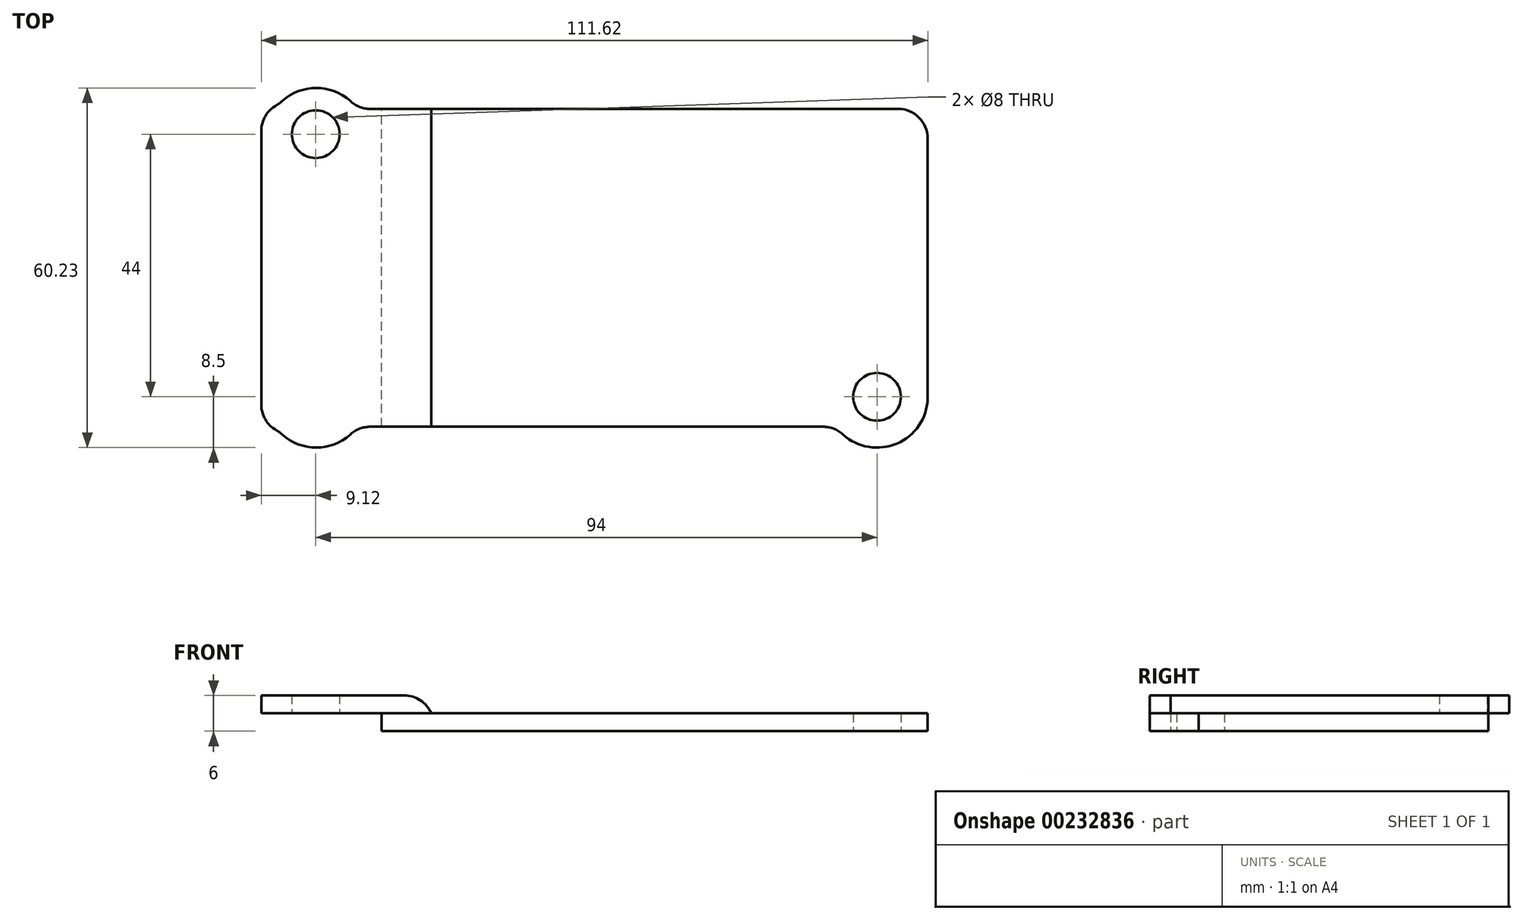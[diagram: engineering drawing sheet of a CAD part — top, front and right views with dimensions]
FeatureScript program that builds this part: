
annotation { "Feature Type Name" : "Feature", "Feature Type Description" : "" }
export const myFeature = defineFeature(function(context is Context, id is Id, definition is map)
    precondition{}
    {
        {
            var Q0;
            Q0=qCreatedBy(makeId("Top.planeOp"),FACE);
            var sketch = newSketch(context, id + "F0", { "sketchPlane" : qUnion([Q0])});
            skCircle(sketch, "E0", {"center": v(0, 0) * mm, "radius": 4 * mm});
            skCircle(sketch, "E1", {"center": v(-94, 0) * mm, "radius": 3.5 * mm, "construction": true});
            skCircle(sketch, "E2", {"center": v(-94, 44) * mm, "radius": 4 * mm});
            skLineSegment(sketch, "E3", {"start": v(-94, 44) * mm, "end": v(-94, 0) * mm, "construction": true});
            skLineSegment(sketch, "E4", {"start": v(-94, 0) * mm, "end": v(0, 0) * mm, "construction": true});
            skLineSegment(sketch, "E5", {"start": v(-94, 44) * mm, "end": v(0, 0) * mm, "construction": true});
            skArc(sketch, "E6", {"start": v(-5.71, -6.3) * mm, "mid": v(3.57, -7.72) * mm, "end": v(8.5, 0.27) * mm});
            skCircle(sketch, "E7", {"center": v(-94, 0) * mm, "radius": 8.5 * mm, "construction": true});
            skLineSegment(sketch, "E8", {"start": v(-83, -5) * mm, "end": v(-9.07, -5) * mm});
            skLineSegment(sketch, "E9", {"start": v(-83, -5) * mm, "end": v(-83, 48.23) * mm});
            skLineSegment(sketch, "E10", {"start": v(8.5, -0.27) * mm, "end": v(8.5, 43.23) * mm});
            skLineSegment(sketch, "E11", {"start": v(3.5, 48.23) * mm, "end": v(-83, 48.23) * mm});
            skPoint(sketch, "E12.visualSharp", {"position": v(8.5, 48.23) * mm});
            skArc(sketch, "E12.filletArc", {"start": v(8.5, 43.23) * mm, "mid": v(7.03, 46.77) * mm, "end": v(3.5, 48.23) * mm});
            skPoint(sketch, "E13.visualSharp", {"position": v(-6.87, -5) * mm});
            skArc(sketch, "E13.filletArc", {"start": v(-5.71, -6.3) * mm, "mid": v(-7.27, -5.34) * mm, "end": v(-9.07, -5) * mm});
            skSolve(sketch);
        }
        {
            var Q0;
            Q0=makeQuery(id+"F0.imprint","IMPRINT",FACE,{"disambiguationData":[TD([[makeQuery(id+"F0.imprint","IMPRINT",EDGE,{"derivedFrom":sQuery(id+"F0.wireOp",EDGE,"E0")}),-1.0]])]});
            extrude(context, id + "F1", {"entities" : qUnion([Q0]), "depth" : 3 * mm});
        }
        {
            var Q0;
            Q0=makeQuery(id+"F1.opExtrude","CAP_FACE",FACE,{"disambiguationData":[OSD([sQuery(id+"F0.wireOp",EDGE,"E0"),sQuery(id+"F0.wireOp",EDGE,"E6"),sQuery(id+"F0.wireOp",EDGE,"E8"),sQuery(id+"F0.wireOp",EDGE,"E9"),sQuery(id+"F0.wireOp",EDGE,"E10"),sQuery(id+"F0.wireOp",EDGE,"E11"),sQuery(id+"F0.wireOp",EDGE,"E12.filletArc"),sQuery(id+"F0.wireOp",EDGE,"E13.filletArc")])],"isStart":false});
            var sketch = newSketch(context, id + "F2", { "sketchPlane" : qUnion([Q0])});
            skLineSegment(sketch, "E14", {"start": v(-74.66, -5) * mm, "end": v(-74.66, 48.23) * mm});
            skLineSegment(sketch, "E15", {"start": v(-74.66, 48.23) * mm, "end": v(-84.85, 48.23) * mm});
            skLineSegment(sketch, "E16", {"start": v(-103.12, 44.5) * mm, "end": v(-103.12, -1.26) * mm});
            skArc(sketch, "E17", {"start": v(-99.63, -6.3) * mm, "mid": v(-93.92, -8.5) * mm, "end": v(-88.2, -6.3) * mm});
            skLineSegment(sketch, "E18.trimOffspring", {"start": v(-84.85, -5) * mm, "end": v(-74.66, -5) * mm});
            skLineSegment(sketch, "E19", {"start": v(-100.8, -5) * mm, "end": v(-100.8, 48.23) * mm, "construction": true});
            skLineSegment(sketch, "E20", {"start": v(-87.04, -5) * mm, "end": v(-87.04, 48.23) * mm, "construction": true});
            skPoint(sketch, "E20.endSnap0", {"position": v(-88.89, 48.23) * mm});
            skArc(sketch, "E21", {"start": v(-88.2, 49.53) * mm, "mid": v(-93.92, 51.73) * mm, "end": v(-99.63, 49.53) * mm});
            skLineSegment(sketch, "E22.trimOffspring", {"start": v(-102.99, 48.23) * mm, "end": v(-103.12, 48.23) * mm});
            skPoint(sketch, "E23.visualSharp", {"position": v(-100.8, 48.23) * mm});
            skArc(sketch, "E23.filletArc", {"start": v(-100.55, 48.87) * mm, "mid": v(-100.07, 49.17) * mm, "end": v(-99.63, 49.53) * mm});
            skArc(sketch, "E24.filletArc", {"start": v(-100.55, 48.87) * mm, "mid": v(-102.43, 47.03) * mm, "end": v(-103.12, 44.5) * mm});
            skPoint(sketch, "E25.visualSharp", {"position": v(-100.8, -5) * mm});
            skArc(sketch, "E25.filletArc", {"start": v(-99.63, -6.3) * mm, "mid": v(-100.07, -5.94) * mm, "end": v(-100.55, -5.63) * mm});
            skArc(sketch, "E26.filletArc", {"start": v(-103.12, -1.26) * mm, "mid": v(-102.43, -3.8) * mm, "end": v(-100.55, -5.63) * mm});
            skPoint(sketch, "E27.visualSharp", {"position": v(-87.04, -5) * mm});
            skArc(sketch, "E27.filletArc", {"start": v(-84.85, -5) * mm, "mid": v(-86.65, -5.34) * mm, "end": v(-88.2, -6.3) * mm});
            skPoint(sketch, "E28.visualSharp", {"position": v(-87.04, 48.23) * mm});
            skArc(sketch, "E28.filletArc", {"start": v(-88.2, 49.53) * mm, "mid": v(-86.65, 48.57) * mm, "end": v(-84.85, 48.23) * mm});
            skSolve(sketch);
        }
        {
            var Q0;
            {var subQ4=sQuery(id+"F2.wireOp",EDGE,"E16");Q0=makeQuery(id+"F2.imprint","IMPRINT",FACE,{"disambiguationData":[TD([[makeQuery(id+"F2.imprint","IMPRINT",EDGE,{"derivedFrom":subQ4}),1.0]])]});}
            var Q1;
            {var subQ0=sQuery(id+"F2.wireOp",EDGE,"E14");Q1=makeQuery(id+"F2.imprint","IMPRINT",FACE,{"disambiguationData":[TD([[makeQuery(id+"F2.imprint","IMPRINT",EDGE,{"derivedFrom":subQ0}),1.0]])]});}
            extrude(context, id + "F3", {"entities" : qUnion([Q0, Q1]), "depth" : 3 * mm});
        }
        {
            var Q0;
            Q0=makeQuery(id+"F0.imprint","IMPRINT",FACE,{"disambiguationData":[TD([[makeQuery(id+"F0.imprint","IMPRINT",EDGE,{"derivedFrom":sQuery(id+"F0.wireOp",EDGE,"E2")}),1.0]])]});
            extrude(context, id + "F4", {"entities" : qUnion([Q0]), "operationType" : NewBodyOperationType.REMOVE, "depth" : 25 * mm});
        }
        {
            var Q0;
            Q0=makeQuery(id+"F3.opExtrude","CAP_EDGE",EDGE,{"disambiguationData":[OSD([sQuery(id+"F2.wireOp",EDGE,"E14")])],"isStart":false});
            fillet(context, id + "F5", {"entities" : qUnion([Q0]), "radius" : 5 * mm, "tangentPropagation" : true, "allowEdgeOverflow" : false});
        }
    });
